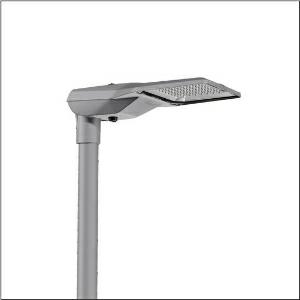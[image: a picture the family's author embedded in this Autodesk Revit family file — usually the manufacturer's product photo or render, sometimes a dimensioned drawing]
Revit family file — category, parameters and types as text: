
# Revit family: streetlight_sl_21_iq_midi___p0_8ab_5xe3r31y08nb_1d5a
name_source: partatom
category: Lighting Fixtures
units: mm (PartAtom-declared; Revit-internal decimal feet)

## family parameters
Cut with Voids When Loaded = No
Host = Face
Light Source = No
Part Type = Normal
Room Calculation Point = No
Round Connector Dimension = Use Diameter
Shared = No

## types (1)
- --- (1 x LED, 18710 lm, 136.6 W, 3000K)
    Apparent Load = 137 VA
    CIE Flux Codes = 39 72 97 100 100
    Color Rendering = 70
    Color Temperature = 3000K
    Default Elevation = 1800 mm
    Description = Streetlight SL 21 iQ midi, mast luminaire, primary light control with lens, of PMMA, primary optical cover: cover, of toughened safety glass, transparent, light distribution: P0.8aB, light emission: direct distribution, primary light characteristic: asymmetric, installation type: post-top, side-entry, LED, High Power LED, rated luminous flux: 18.710lm, luminous efficacy: 137lm/W, light colour: 730, colour temperature: 3000K, control gear: iQ-Street Remote, D4i with power reduction, control: pre-setting: logarithmic dimming characteristic, Street-Remote, Auto-Match, Temp-Guard, Lumen-Switch, Night-Set, Smart-Wire, Light-Fading, Desk-Remote (wireless, voltage-free reading and setting of iQ features in the workshop via application-optimized NFC function/RFID function), optimised constant luminous flux control (CLO 2.0), mains connection: 230..240V, AC, 50/60Hz, start of lifetime: 137W, end of service life: 144W, reduction: 61W, luminaire housing, of diecast aluminium, powder-coated, Siteco® metallic grey (DB 702S), corrosivity category C5 mid according to DIN EN ISO 12944, please order mast flange separately, inclination adjustable: 0°, 5°, 10°, 15°, sealing non-destructively replaceable, multi-level sealing system, length: 644mm, width: 335mm, height: 110mm, mast flange for spigot size: 42mm (side-entry): 5XC10008XM4, 60/48mm (side-entry/post-top): 5XC10108XM2, 76/60mm (side-entry/post-top): 5XC10108XM1, mounting height: 4..8m, Smart Interface below and above, protection rating (complete): IP66, insulation class (complete): insulation class II (safety insulation), certification: CE, ENEC, ENEC+, VDE, impact resistance: IK10, permissible operating ambient temperature for outdoor applications: -40..+50°C, standard-compliant lighting for roads and squares, packaging unit: 1 piece

Light Distribution: P0.8aB
    Height = 111 mm
    Lamp = 1 x LED
    Lamp Light Flux = 18710 lm
    Lamp Power = 136.6 W
    Lamp count = 1
    Length = 644 mm
    Luminous efficacy = 137 lm/W
    Manufacturer = Siteco
    ModVariant = No
    Model = 5XE3R31Y08NB
    Number of Poles = 1
    OnlyDefault = Yes
    Power Factor = 1
    Product Name = Streetlight SL 21 iQ midi | P0.8aB
    Product group = mast luminaire | pylon top
    ProductGroupID = 6100
    Protection Class = Protection class II
    Protection Degree = IP 66
    RLX_Detail_Level = 1
    RLX_Emergency_Light_Flux = 0 lm
    RLX_Emergency_Type = 0
    RLX_Emergency_Type_DB = No
    RlxData = <blob elided: 90553 chars, md5=2de5d836>
    Socket = socket
    Standby Power = 0 W
    System Light Flux = 18710 lm
    System Power = 137 W
    Type Comments = factory setting: luminous flux: 100 % | dim-lin: 254 | 733 mA
    Type Image = l_1004304.jpg
    URL = http://relux.com
    VarID = @adj_092697
    Voltage = 0 V
    Weight = 0.00 kg
    Width = 336 mm

## geometry (parser evidence)
native form markers: Blend x4, Sweep x12
no freeform markers — native parametric forms only
